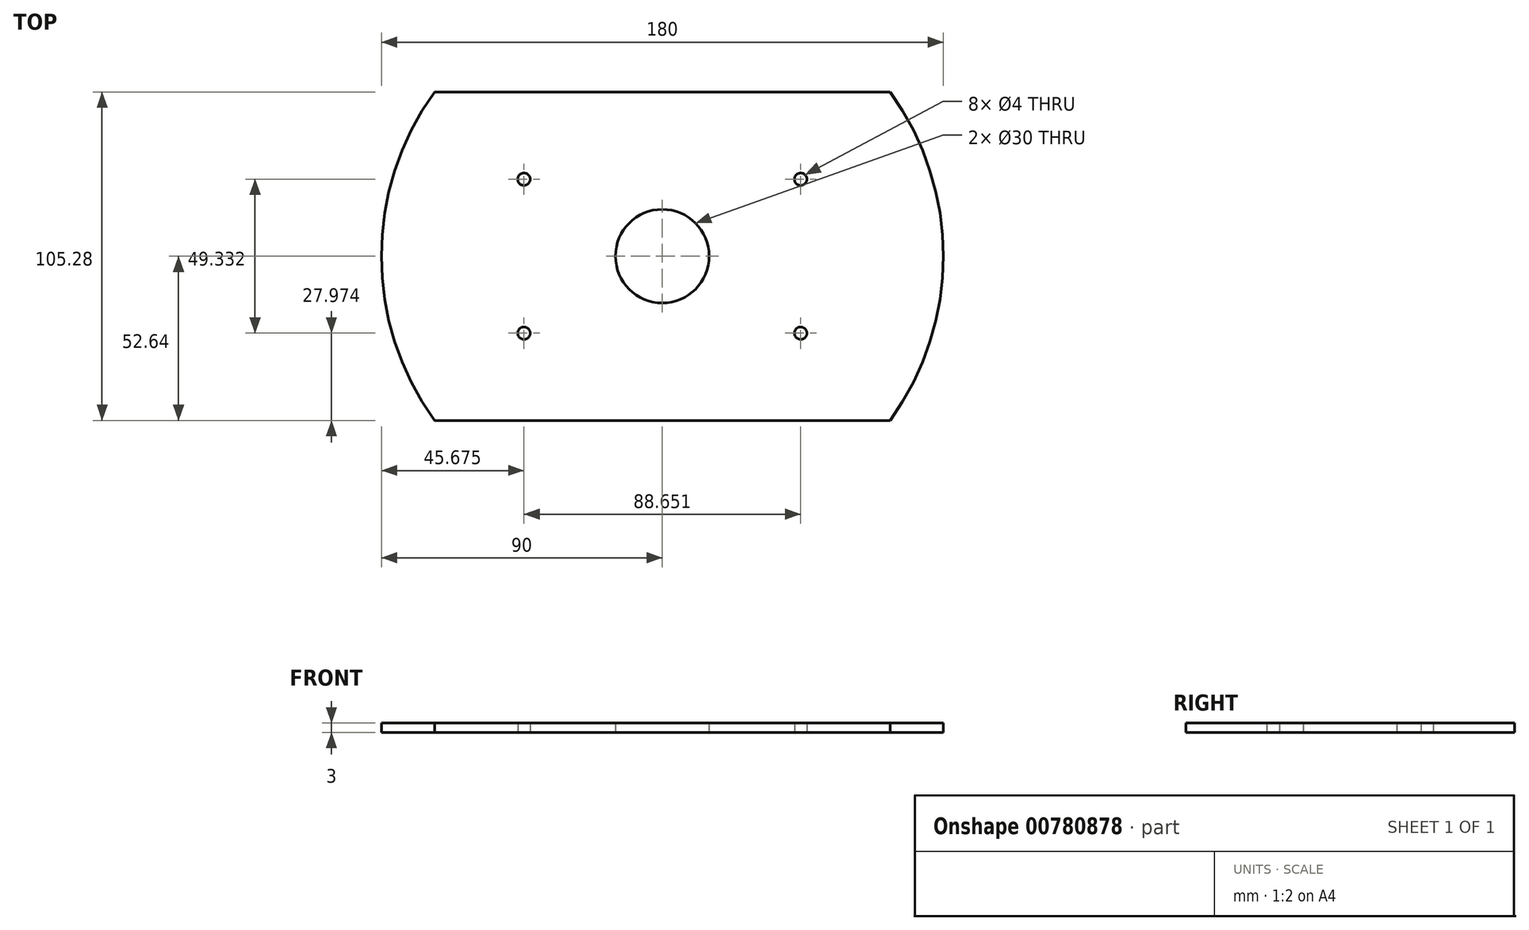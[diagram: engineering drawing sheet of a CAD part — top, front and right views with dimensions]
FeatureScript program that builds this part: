
annotation { "Feature Type Name" : "Feature", "Feature Type Description" : "" }
export const myFeature = defineFeature(function(context is Context, id is Id, definition is map)
    precondition{}
    {
        {
            var Q0;
            Q0=qCreatedBy(makeId("Top.planeOp"),FACE);
            var sketch = newSketch(context, id + "F0", { "sketchPlane" : qUnion([Q0])});
            skCircle(sketch, "E0", {"center": v(0, 0) * mm, "radius": 90 * mm});
            skCircle(sketch, "E1", {"center": v(-44.33, 24.67) * mm, "radius": 2 * mm});
            skCircle(sketch, "E2.MirrorC", {"center": v(-44.33, -24.67) * mm, "radius": 2 * mm});
            skCircle(sketch, "E3.MirrorC", {"center": v(44.33, 24.67) * mm, "radius": 2 * mm});
            skCircle(sketch, "E4.MirrorC", {"center": v(44.33, -24.67) * mm, "radius": 2 * mm});
            skLineSegment(sketch, "E5", {"start": v(-73, 52.64) * mm, "end": v(73, 52.64) * mm});
            skLineSegment(sketch, "E6.MirrorCS", {"start": v(-73, -52.64) * mm, "end": v(73, -52.64) * mm});
            skCircle(sketch, "E7", {"center": v(0, 0) * mm, "radius": 15 * mm});
            skSolve(sketch);
        }
        {
            var Q0;
            Q0=makeQuery(id+"F0.imprint","IMPRINT",FACE,{"disambiguationData":[TD([[makeQuery(id+"F0.imprint","IMPRINT",EDGE,{"derivedFrom":sQuery(id+"F0.wireOp",EDGE,"E1")}),-1.0]])]});
            extrude(context, id + "F1", {"entities" : qUnion([Q0]), "depth" : 3 * mm, "offsetDistance" : 25 * mm});
        }
    });
